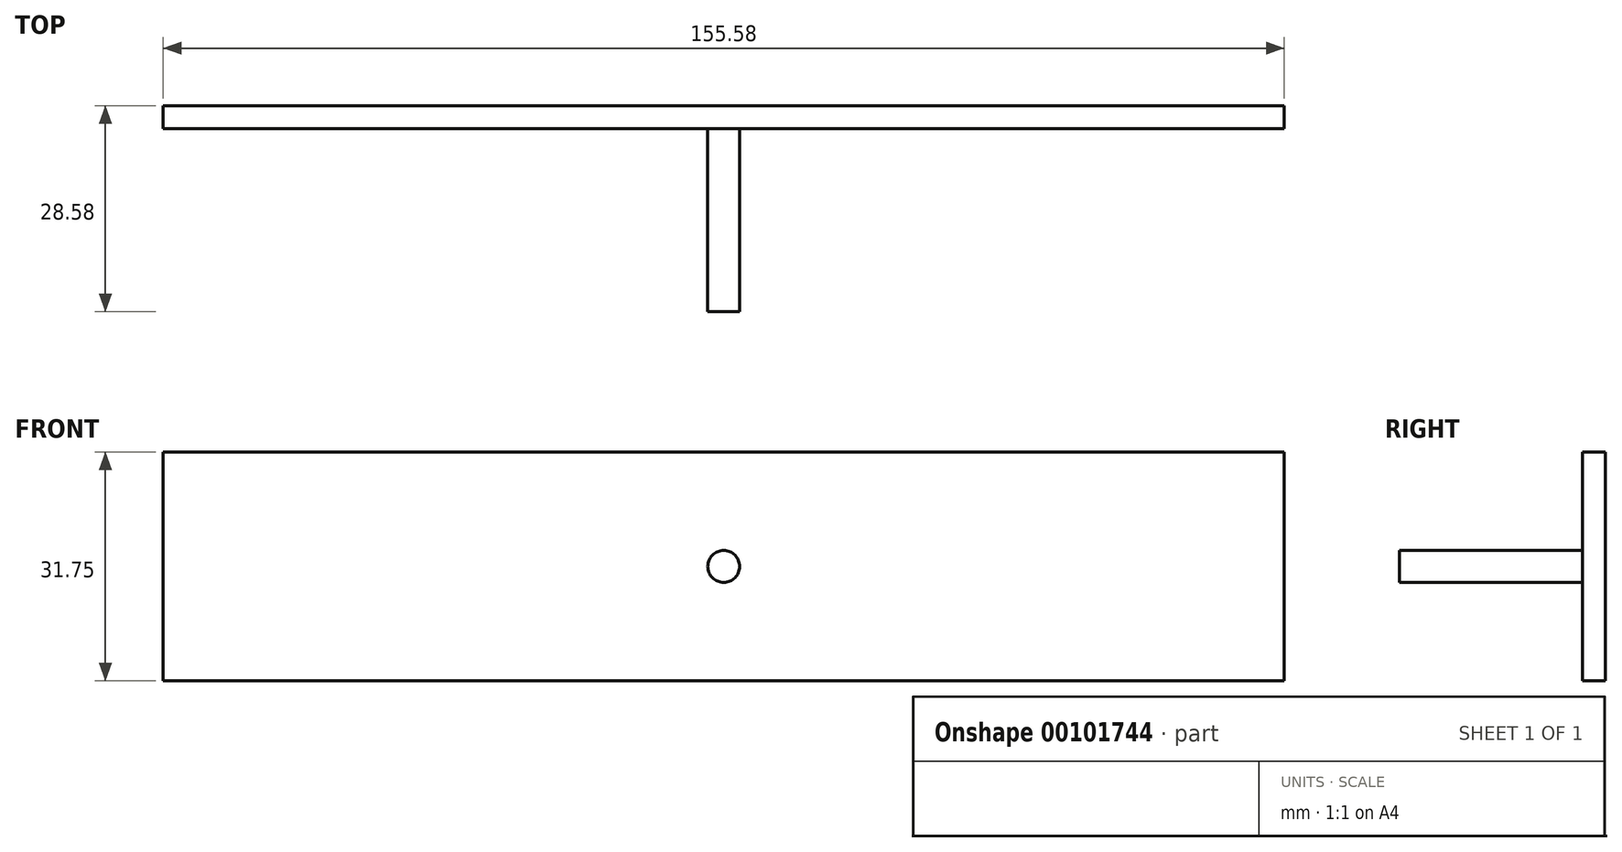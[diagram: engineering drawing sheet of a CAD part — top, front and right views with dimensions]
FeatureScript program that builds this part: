
annotation { "Feature Type Name" : "Feature", "Feature Type Description" : "" }
export const myFeature = defineFeature(function(context is Context, id is Id, definition is map)
    precondition{}
    {
        {
            var Q0;
            Q0=qCreatedBy(makeId("Front.planeOp"),FACE);
            var sketch = newSketch(context, id + "F0", { "sketchPlane" : qUnion([Q0])});
            skLineSegment(sketch, "E0.bottom", {"start": v(-39.18, 47.82) * mm, "end": v(116.4, 47.82) * mm});
            skLineSegment(sketch, "E0.top", {"start": v(-39.18, 16.07) * mm, "end": v(116.4, 16.07) * mm});
            skLineSegment(sketch, "E0.left", {"start": v(-39.18, 47.82) * mm, "end": v(-39.18, 16.07) * mm});
            skLineSegment(sketch, "E0.right", {"start": v(116.4, 47.82) * mm, "end": v(116.4, 16.07) * mm});
            skPoint(sketch, "E1", {"position": v(38.61, 47.82) * mm});
            skPoint(sketch, "E2", {"position": v(38.61, 16.07) * mm});
            skPoint(sketch, "E3", {"position": v(-39.18, 31.94) * mm});
            skPoint(sketch, "E4", {"position": v(116.4, 31.94) * mm});
            skLineSegment(sketch, "E5", {"start": v(38.61, 47.82) * mm, "end": v(38.61, 16.07) * mm});
            skPoint(sketch, "E6", {"position": v(38.61, 31.94) * mm});
            skSolve(sketch);
        }
        {
            var Q0;
            Q0=qSketchRegion(id+"F0",true);
            extrude(context, id + "F1", {"entities" : qUnion([Q0]), "depth" : 3.17 * mm});
        }
        {
            var Q0;
            Q0=makeQuery(id+"F1.opExtrude","CAP_FACE",FACE,{"disambiguationData":[OSD([sQuery(id+"F0.wireOp",EDGE,"E0.bottom"),sQuery(id+"F0.wireOp",EDGE,"E0.top"),sQuery(id+"F0.wireOp",EDGE,"E0.left"),sQuery(id+"F0.wireOp",EDGE,"E0.right")])],"isStart":false});
            var sketch = newSketch(context, id + "F2", { "sketchPlane" : qUnion([Q0])});
            skSolve(sketch);
        }
        {
            var Q0;
            Q0=makeQuery(id+"F2.imprint","IMPRINT",FACE,{"disambiguationData":[TD([[makeQuery(id+"F2.imprint","IMPRINT",EDGE,{"derivedFrom":makeQuery(id+"F1.opExtrude","CAP_EDGE",EDGE,{"disambiguationData":[OSD([sQuery(id+"F0.wireOp",EDGE,"E0.bottom")])],"isStart":false})}),-1.0]])]});
            var sketch = newSketch(context, id + "F3", { "sketchPlane" : qUnion([Q0])});
            skCircle(sketch, "E7", {"center": v(38.61, 31.95) * mm, "radius": 2.2 * mm});
            skSolve(sketch);
        }
        {
            var Q0;
            Q0 = qSketchRegion(id + "F3", true);
            extrude(context, id + "F4", {"entities" : qUnion([Q0]), "operationType" : NewBodyOperationType.ADD, "depth" : 25.4 * mm});
        }
    });
